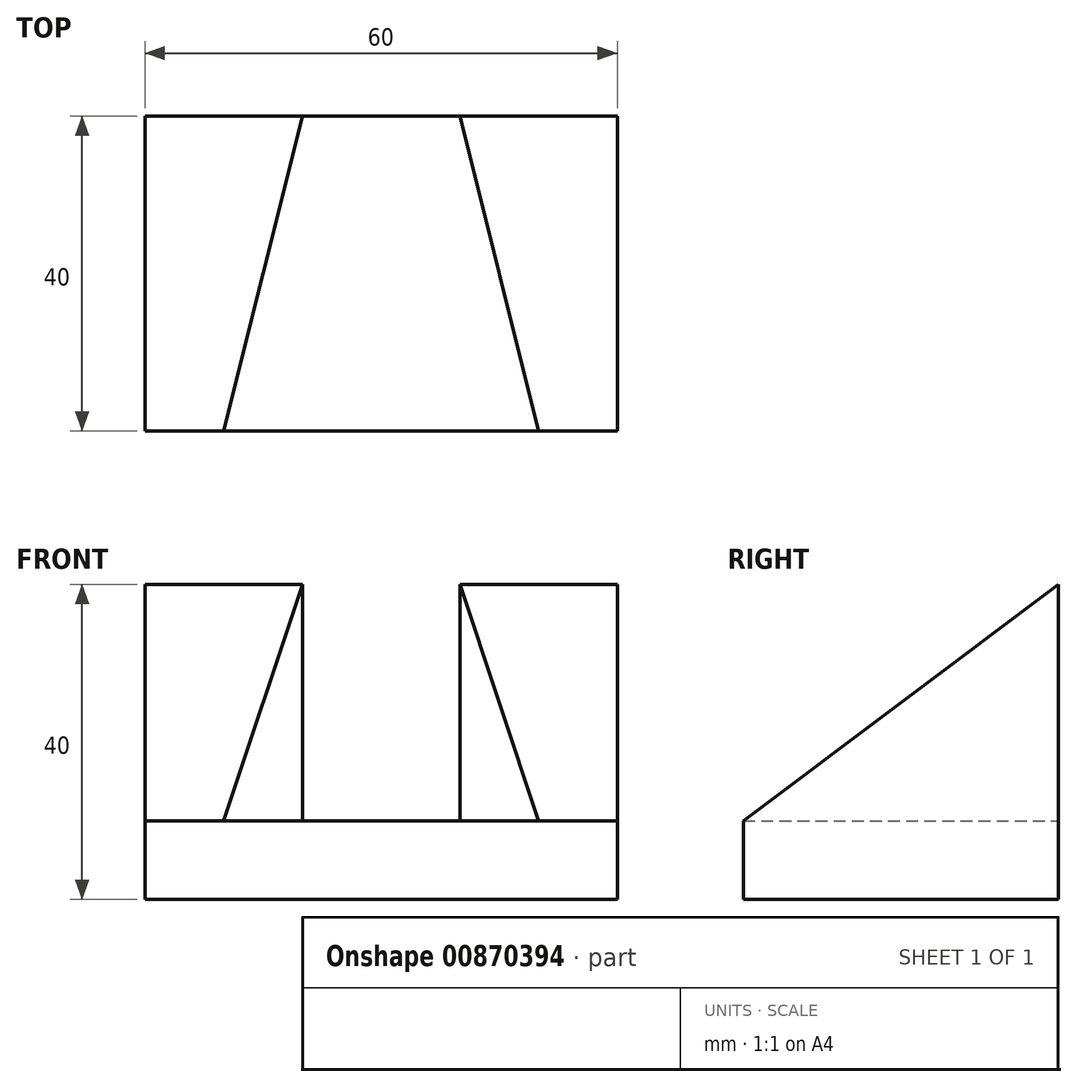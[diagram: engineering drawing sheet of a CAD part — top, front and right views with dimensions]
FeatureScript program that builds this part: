
annotation { "Feature Type Name" : "Feature", "Feature Type Description" : "" }
export const myFeature = defineFeature(function(context is Context, id is Id, definition is map)
    precondition{}
    {
        {
            var Q0;
            Q0=qCreatedBy(makeId("Top.planeOp"),FACE);
            var sketch = newSketch(context, id + "F0", { "sketchPlane" : qUnion([Q0])});
            skLineSegment(sketch, "E0.bottom", {"start": v(-30, 0) * mm, "end": v(30, 0) * mm});
            skLineSegment(sketch, "E0.top", {"start": v(-30, 40) * mm, "end": v(30, 40) * mm});
            skLineSegment(sketch, "E0.left", {"start": v(-30, 0) * mm, "end": v(-30, 40) * mm});
            skLineSegment(sketch, "E0.right", {"start": v(30, 0) * mm, "end": v(30, 40) * mm});
            skSolve(sketch);
        }
        {
            var Q0;
            Q0 = qSketchRegion(id + "F0", true);
            extrude(context, id + "F1", {"entities" : qUnion([Q0]), "depth" : 40 * mm, "offsetDistance" : 25 * mm});
        }
        {
            var Q0;
            Q0=makeQuery(id+"F1.opExtrude","CAP_FACE",FACE,{"disambiguationData":[OSD([sQuery(id+"F0.wireOp",EDGE,"E0.bottom"),sQuery(id+"F0.wireOp",EDGE,"E0.top"),sQuery(id+"F0.wireOp",EDGE,"E0.left"),sQuery(id+"F0.wireOp",EDGE,"E0.right")])],"isStart":false});
            var sketch = newSketch(context, id + "F2", { "sketchPlane" : qUnion([Q0])});
            skLineSegment(sketch, "E1", {"start": v(-20, 0) * mm, "end": v(20, 0) * mm});
            skLineSegment(sketch, "E2", {"start": v(20, 0) * mm, "end": v(10, 40) * mm});
            skLineSegment(sketch, "E3", {"start": v(10, 40) * mm, "end": v(-10, 40) * mm});
            skLineSegment(sketch, "E4", {"start": v(-10, 40) * mm, "end": v(-20, 0) * mm});
            skSolve(sketch);
        }
        {
            var Q0;
            Q0 = qSketchRegion(id + "F2", true);
            extrude(context, id + "F3", {"entities" : qUnion([Q0]), "operationType" : NewBodyOperationType.REMOVE, "oppositeDirection" : true, "depth" : 30 * mm, "offsetDistance" : 25 * mm});
        }
        {
            var Q0;
            {var subQ0=sQuery(id+"F0.wireOp",EDGE,"E0.bottom");var subQ1=sQuery(id+"F0.wireOp",EDGE,"E0.left");Q0=makeQuery(id+"F3.boolean.opBoolean","SPLIT",EDGE,{"disambiguationData":[TD([makeQuery(id+"F1.opExtrude","SWEPT_FACE",FACE,{"disambiguationData":[OSD([subQ1])]})])],"derivedFrom":makeQuery(id+"F1.opExtrude","CAP_EDGE",EDGE,{"disambiguationData":[OSD([subQ0])],"isStart":false})});}
            var Q1;
            {var subQ0=sQuery(id+"F0.wireOp",EDGE,"E0.bottom");var subQ1=sQuery(id+"F0.wireOp",EDGE,"E0.right");Q1=makeQuery(id+"F3.boolean.opBoolean","SPLIT",EDGE,{"disambiguationData":[TD([makeQuery(id+"F1.opExtrude","SWEPT_FACE",FACE,{"disambiguationData":[OSD([subQ1])]})])],"derivedFrom":makeQuery(id+"F1.opExtrude","CAP_EDGE",EDGE,{"disambiguationData":[OSD([subQ0])],"isStart":false})});}
            chamfer(context, id + "F4", {"entities" : qUnion([Q0, Q1]), "chamferType" : ChamferType.TWO_OFFSETS, "width1" : 40 * mm, "oppositeDirection" : false, "width2" : 30 * mm, "tangentPropagation" : true});
        }
    });
